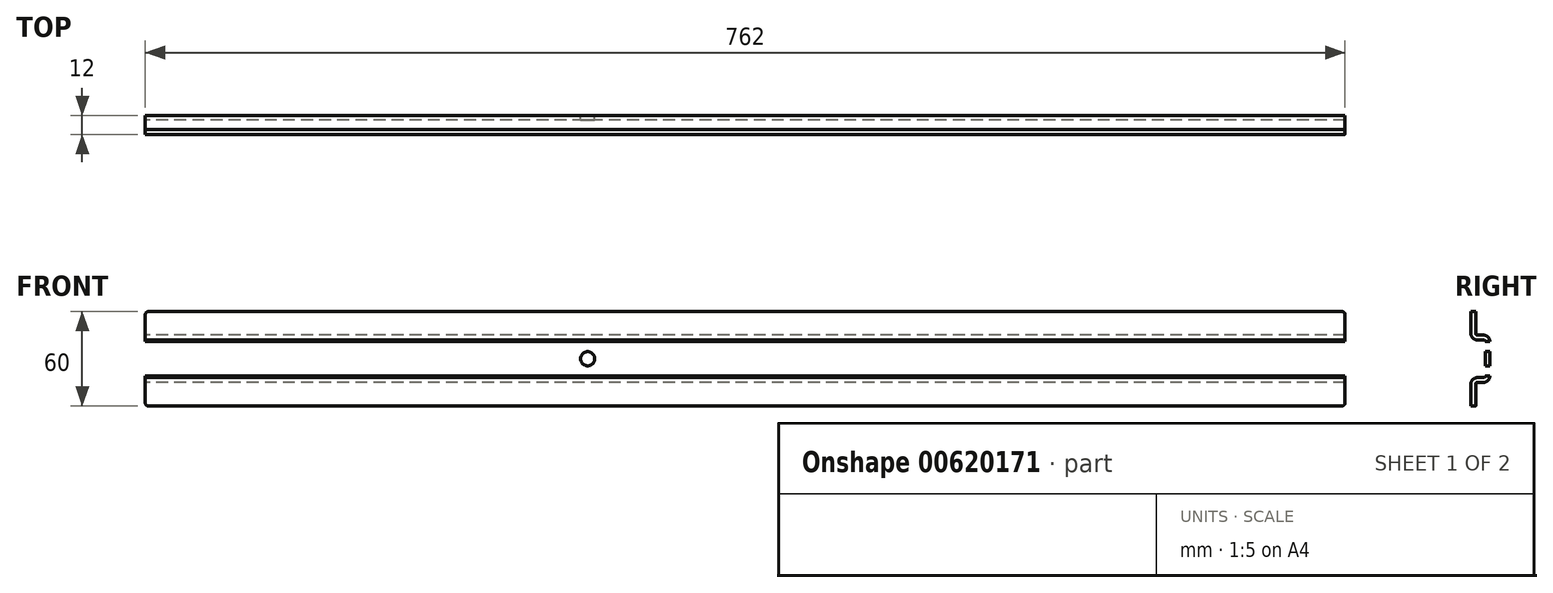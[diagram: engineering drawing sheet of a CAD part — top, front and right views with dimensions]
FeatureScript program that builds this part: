
annotation { "Feature Type Name" : "Feature", "Feature Type Description" : "" }
export const myFeature = defineFeature(function(context is Context, id is Id, definition is map)
    precondition{}
    {
        {
            var Q0;
            Q0=qCreatedBy(makeId("Right.planeOp"),FACE);
            var sketch = newSketch(context, id + "F0", { "sketchPlane" : qUnion([Q0])});
            skLineSegment(sketch, "E0", {"start": v(0, 0) * mm, "end": v(0, 11) * mm});
            skLineSegment(sketch, "E1", {"start": v(-4, 15) * mm, "end": v(-8, 15) * mm});
            skLineSegment(sketch, "E2", {"start": v(-9, 16) * mm, "end": v(-9, 30) * mm});
            skLineSegment(sketch, "E3", {"start": v(-9, 30) * mm, "end": v(-12, 30) * mm});
            skLineSegment(sketch, "E4", {"start": v(-12, 30) * mm, "end": v(-12, 16) * mm});
            skLineSegment(sketch, "E5", {"start": v(-8, 12) * mm, "end": v(-4, 12) * mm});
            skLineSegment(sketch, "E6", {"start": v(-3, 11) * mm, "end": v(-3, 0) * mm});
            skPoint(sketch, "E7.visualSharp", {"position": v(-9, 15) * mm});
            skArc(sketch, "E7.filletArc", {"start": v(-9, 16) * mm, "mid": v(-8.7, 15.3) * mm, "end": v(-8, 15) * mm});
            skPoint(sketch, "E8.visualSharp", {"position": v(-3, 12) * mm});
            skArc(sketch, "E8.filletArc", {"start": v(-3, 11) * mm, "mid": v(-3.3, 11.7) * mm, "end": v(-4, 12) * mm});
            skPoint(sketch, "E9.visualSharp", {"position": v(0, 15) * mm});
            skArc(sketch, "E9.filletArc", {"start": v(0, 11) * mm, "mid": v(-1.17, 13.83) * mm, "end": v(-4, 15) * mm});
            skPoint(sketch, "E10.visualSharp", {"position": v(-12, 12) * mm});
            skArc(sketch, "E10.filletArc", {"start": v(-12, 16) * mm, "mid": v(-10.83, 13.17) * mm, "end": v(-8, 12) * mm});
            skLineSegment(sketch, "E11.MirrorCS", {"start": v(0, 0) * mm, "end": v(0, -11) * mm});
            skArc(sketch, "E12.MirrorCS", {"start": v(0, -11) * mm, "mid": v(-1.17, -13.83) * mm, "end": v(-4, -15) * mm});
            skLineSegment(sketch, "E13.MirrorCS", {"start": v(-4, -15) * mm, "end": v(-8, -15) * mm});
            skArc(sketch, "E14.MirrorCS", {"start": v(-9, -16) * mm, "mid": v(-8.7, -15.3) * mm, "end": v(-8, -15) * mm});
            skLineSegment(sketch, "E15.MirrorCS", {"start": v(-9, -16) * mm, "end": v(-9, -30) * mm});
            skLineSegment(sketch, "E16.MirrorCS", {"start": v(-9, -30) * mm, "end": v(-12, -30) * mm});
            skLineSegment(sketch, "E17.MirrorCS", {"start": v(-12, -30) * mm, "end": v(-12, -16) * mm});
            skArc(sketch, "E18.MirrorCS", {"start": v(-12, -16) * mm, "mid": v(-10.83, -13.17) * mm, "end": v(-8, -12) * mm});
            skLineSegment(sketch, "E19.MirrorCS", {"start": v(-8, -12) * mm, "end": v(-4, -12) * mm});
            skArc(sketch, "E20.MirrorCS", {"start": v(-3, -11) * mm, "mid": v(-3.3, -11.7) * mm, "end": v(-4, -12) * mm});
            skLineSegment(sketch, "E21.MirrorCS", {"start": v(-3, -11) * mm, "end": v(-3, 0) * mm});
            skSolve(sketch);
        }
        {
            var Q0;
            Q0=makeQuery(id+"F0.imprint","IMPRINT",FACE,{"disambiguationData":[TD([[makeQuery(id+"F0.imprint","IMPRINT",EDGE,{"derivedFrom":sQuery(id+"F0.wireOp",EDGE,"E0")}),1.0]])]});
            extrude(context, id + "F1", {"entities" : qUnion([Q0]), "endBound" : BoundingType.SYMMETRIC, "depth" : 762 * mm, "offsetDistance" : 25 * mm});
        }
        {
            var Q0;
            Q0=makeQuery(id+"F1.opExtrude","SWEPT_FACE",FACE,{"disambiguationData":[OSD([sQuery(id+"F0.wireOp",EDGE,"E0"),sQuery(id+"F0.wireOp",EDGE,"E11.MirrorCS")])]});
            var sketch = newSketch(context, id + "F2", { "sketchPlane" : qUnion([Q0])});
            skCircle(sketch, "E22", {"center": v(-100, 0) * mm, "radius": 4.5 * mm});
            skCircle(sketch, "E23.MirrorC", {"center": v(100, 0) * mm, "radius": 4.5 * mm});
            skSolve(sketch);
        }
        {
            var Q0;
            Q0=makeQuery(id+"F2.imprint","IMPRINT",FACE,{"disambiguationData":[TD([[makeQuery(id+"F2.imprint","IMPRINT",EDGE,{"derivedFrom":sQuery(id+"F2.wireOp",EDGE,"E22")}),1.0]])]});
            var Q1;
            Q1=makeQuery(id+"F2.imprint","IMPRINT",FACE,{"disambiguationData":[TD([[makeQuery(id+"F2.imprint","IMPRINT",EDGE,{"derivedFrom":sQuery(id+"F2.wireOp",EDGE,"E23.MirrorC")}),-1.0]])]});
            extrude(context, id + "F3", {"entities" : qUnion([Q0, Q1]), "operationType" : NewBodyOperationType.REMOVE, "endBound" : BoundingType.THROUGH_ALL, "oppositeDirection" : true, "depth" : 25 * mm, "offsetDistance" : 25 * mm});
        }
        {
            var Q0;
            Q0=makeQuery(id+"F1.opExtrude","CAP_EDGE",EDGE,{"disambiguationData":[OSD([sQuery(id+"F0.wireOp",EDGE,"E3")])],"isStart":true});
            var Q1;
            Q1=makeQuery(id+"F1.opExtrude","CAP_EDGE",EDGE,{"disambiguationData":[OSD([sQuery(id+"F0.wireOp",EDGE,"E16.MirrorCS")])],"isStart":true});
            var Q2;
            Q2=makeQuery(id+"F1.opExtrude","CAP_EDGE",EDGE,{"disambiguationData":[OSD([sQuery(id+"F0.wireOp",EDGE,"E3")])],"isStart":false});
            var Q3;
            Q3=makeQuery(id+"F1.opExtrude","CAP_EDGE",EDGE,{"disambiguationData":[OSD([sQuery(id+"F0.wireOp",EDGE,"E16.MirrorCS")])],"isStart":false});
            fillet(context, id + "F4", {"entities" : qUnion([Q0, Q1, Q2, Q3]), "radius" : 2 * mm, "tangentPropagation" : true, "allowEdgeOverflow" : false});
        }
    });
